# Revit family: G庇 ポール付き
name_source: partatom
category: 一般モデル
units: mm (PartAtom-declared; Revit-internal decimal feet)

## family parameters
パーツ タイプ = 標準
ホスト = 面
ロード時にボイドで切り取り = いいえ
丸型コネクタ寸法 = 直径を使用
共有 = いいえ
部屋計算ポイント = いいえ
鉄筋をホスト可能 = いいえ

## types (1)
- G庇 ポール付き
    A = 7947
    B = 1720
    G庇D寸法 = 2500  [stored 8.2021 ft]
    G庇L寸法 = 8000  [stored 26.2467 ft]
    URL = https://tuzuki.co.jp
    サポートポール数 = 6
    サポートポール＠ = 1500  [stored 4.92126 ft]
    パネル吊元-躯体間距離 = 28
    パネル長さ差分 = 53
    ポール@1000mm = いいえ
    ポール@1500mm = はい
    ポールL寸法 = 1951
    ポール取付高さ = 1100
    モデル = グロンダート　Gシリーズ（サポートポール付）
    先端部材1 = いいえ
    先端部材1 断面表示 = いいえ
    先端部材2 = はい
    先端部材2 断面表示 = いいえ
    先端部材長さ = 0  [stored 0 ft]
    基準サポートポール@ = 1500  [stored 4.92126 ft]
    実G庇D寸法 = 2500  [stored 8.2021 ft]
    庇 色 = アルミニウム 6063S-T5 シルバー(R) (株)ツヅキ
    断面図表記 上ブラケット小 = はい
    断面図表記 上部ブラケット大 = いいえ
    断面図表記 先端部材1 = いいえ
    断面図表記 先端部材2 = はい
    既定の高さ = 1000  [stored 3.28084 ft]
    製造元 = 株式会社ツヅキ
    説明 = 前方からの雨垂れをなくし、壁面側より雨水を排出できる機能を持つ内勾配庇です。デザインタイプの先端部分を両サイドまで回り込ませた三方枠も好評!

note: [stored X ft] marks values corroborated as IEEE doubles in the binary element streams (Revit-internal decimal feet)
